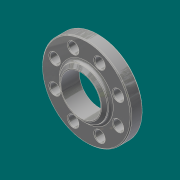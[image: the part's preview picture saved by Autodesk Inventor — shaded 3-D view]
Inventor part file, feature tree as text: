
AUTODESK INVENTOR PART (.ipt)
format: ipt  version: 2017.3 (Build 213257000, 257)  size: 193,024 bytes
history: native  units: in
note: dims shown in document units (in); Inventor stores cm internally (conversion verified against a paired STEP export)
features: chamfer x2, sketch x2, revolve x1, hole x1, pattern_circular x1
ambient origin geometry x8: Origin, YZ Plane, XZ Plane, XY Plane, X Axis, Y Axis, Z Axis, Center Point
bodies: Solid1 (feature_tree)
feature tree (7):
  revolve  "Revolution1"  [1 undecoded]
  hole  "Hole1"  [1 undecoded]
  chamfer  "Chamfer1"  Distance=0.0625in
  pattern_circular  "Circular Pattern1"  [2 undecoded]
  chamfer  "Chamfer2"  Distance=2.9in
  sketch  "Sketch1"  dims[d0=1.3438in d1=6.5in]
  sketch  "Sketch2"  dims[d2=0.9375in d3=3.625in d4=0.0625in d5=3.5in d6=2.9in d7=3.61in d8=0.2577in d9=0.2375in d10=0.2in d11=90.0deg d12=5.0in d13=22.5deg d14=0.75in d15=0.75in d16=0.375in d17=0.25in d18=0.5635in d19=1.0in d20=0.8108in d21=0.0469in d22=0.125in d23=45.0deg d24=3.1496in d25=360.0deg d27=0.0625in d28=0.125in d29=45.0deg]
note: 4 required parameter values undecoded (feature->parameter linkage not recoverable at this tier; creation-order binding heuristic only, values carry confidence <= 0.55)